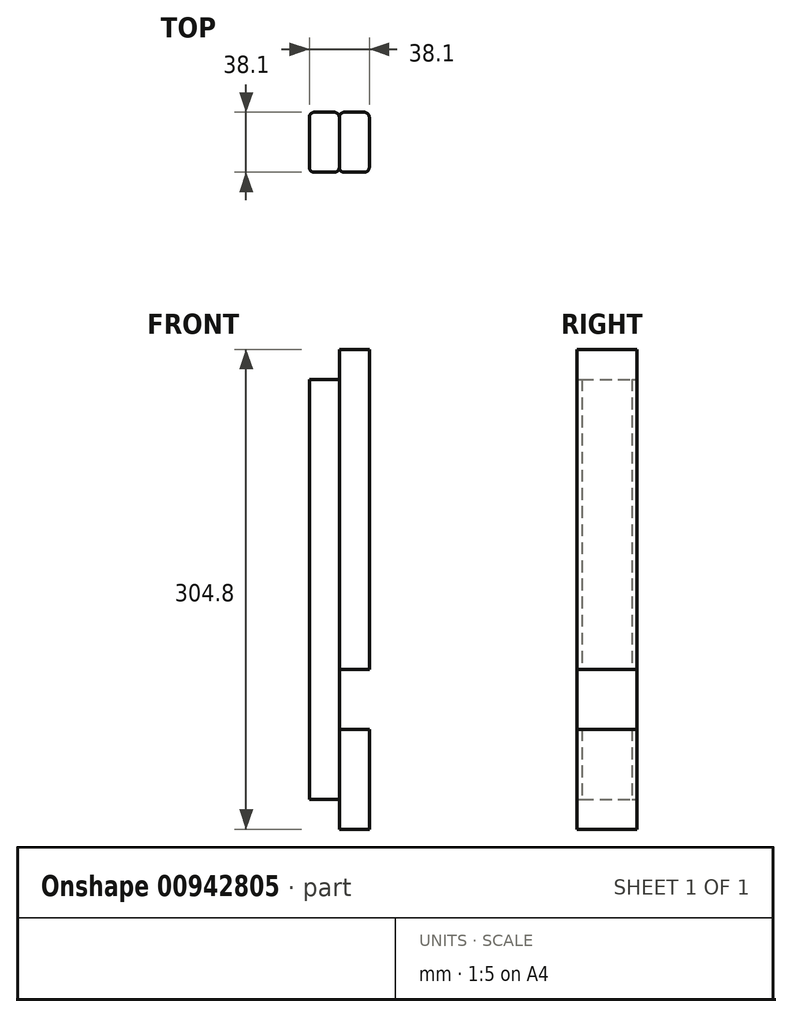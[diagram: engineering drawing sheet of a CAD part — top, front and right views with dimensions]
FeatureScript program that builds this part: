
annotation { "Feature Type Name" : "Feature", "Feature Type Description" : "" }
export const myFeature = defineFeature(function(context is Context, id is Id, definition is map)
    precondition{}
    {
        {
            var Q0;
            Q0=qCreatedBy(makeId("Top.planeOp"),FACE);
            var sketch = newSketch(context, id + "F0", { "sketchPlane" : qUnion([Q0])});
            skLineSegment(sketch, "E0.bottom", {"start": v(3.15, 0) * mm, "end": v(15.9, 0) * mm});
            skLineSegment(sketch, "E0.top", {"start": v(3.15, 38.1) * mm, "end": v(15.9, 38.1) * mm});
            skLineSegment(sketch, "E0.left", {"start": v(0, 3.15) * mm, "end": v(0, 34.95) * mm});
            skLineSegment(sketch, "E0.right", {"start": v(19.05, 3.15) * mm, "end": v(19.05, 34.95) * mm});
            skPoint(sketch, "E1.visualSharp", {"position": v(0, 38.1) * mm});
            skArc(sketch, "E1.filletArc", {"start": v(3.15, 38.1) * mm, "mid": v(0.92, 37.18) * mm, "end": v(0, 34.95) * mm});
            skArc(sketch, "E2.filletArc", {"start": v(19.05, 34.95) * mm, "mid": v(18.13, 37.18) * mm, "end": v(15.9, 38.1) * mm});
            skPoint(sketch, "E3.visualSharp", {"position": v(19.05, 0) * mm});
            skArc(sketch, "E3.filletArc", {"start": v(15.9, 0) * mm, "mid": v(18.13, 0.92) * mm, "end": v(19.05, 3.15) * mm});
            skPoint(sketch, "E4.visualSharp", {"position": v(0, 0) * mm});
            skArc(sketch, "E4.filletArc", {"start": v(0, 3.15) * mm, "mid": v(0.92, 0.92) * mm, "end": v(3.15, 0) * mm});
            skLineSegment(sketch, "E5.bottom", {"start": v(22.2, 0) * mm, "end": v(34.95, 0) * mm});
            skLineSegment(sketch, "E5.right", {"start": v(38.1, 3.15) * mm, "end": v(38.1, 34.95) * mm});
            skArc(sketch, "E6.filletArc", {"start": v(22.2, 38.1) * mm, "mid": v(19.97, 37.18) * mm, "end": v(19.05, 34.95) * mm});
            skArc(sketch, "E7.filletArc", {"start": v(38.1, 34.95) * mm, "mid": v(37.18, 37.18) * mm, "end": v(34.95, 38.1) * mm});
            skArc(sketch, "E8.filletArc", {"start": v(34.95, 0) * mm, "mid": v(37.18, 0.92) * mm, "end": v(38.1, 3.15) * mm});
            skArc(sketch, "E9.filletArc", {"start": v(19.05, 3.15) * mm, "mid": v(19.97, 0.92) * mm, "end": v(22.2, 0) * mm});
            skLineSegment(sketch, "E10", {"start": v(22.2, 38.1) * mm, "end": v(34.95, 38.1) * mm});
            skSolve(sketch);
        }
        {
            var Q0;
            Q0=makeQuery(id+"F0.imprint","IMPRINT",FACE,{"disambiguationData":[TD([[makeQuery(id+"F0.imprint","IMPRINT",EDGE,{"derivedFrom":sQuery(id+"F0.wireOp",EDGE,"E5.bottom")}),1.0]])]});
            var Q1;
            Q1=makeQuery(id+"F0.imprint","IMPRINT",FACE,{"disambiguationData":[TD([[makeQuery(id+"F0.imprint","IMPRINT",EDGE,{"derivedFrom":sQuery(id+"F0.wireOp",EDGE,"b7ff1907-7b2b-4cdd-8ea5-b45dade5522d.bottom")}),1.0]])]});
            var Q2;
            Q2=makeQuery(id+"F0.imprint","IMPRINT",FACE,{"disambiguationData":[TD([[makeQuery(id+"F0.imprint","IMPRINT",EDGE,{"derivedFrom":sQuery(id+"F0.wireOp",EDGE,"66c86851-db75-4c71-9093-7621e61d7ab7.bottom")}),1.0]])]});
            extrude(context, id + "F1", {"entities" : qUnion([Q0, Q1, Q2]), "depth" : 304.8 * mm, "offsetDistance" : 25.4 * mm});
        }
        {
            var Q0;
            Q0=qSketchRegion(id+"F0",true);
            extrude(context, id + "F2", {"entities" : qUnion([Q0]), "operationType" : NewBodyOperationType.ADD, "depth" : 285.75 * mm, "offsetDistance" : 25.4 * mm});
        }
        {
            var Q0;
            Q0=makeQuery(id+"F0.imprint","IMPRINT",FACE,{"disambiguationData":[TD([[makeQuery(id+"F0.imprint","IMPRINT",EDGE,{"derivedFrom":sQuery(id+"F0.wireOp",EDGE,"E0.bottom")}),1.0]])]});
            extrude(context, id + "F3", {"entities" : qUnion([Q0]), "operationType" : NewBodyOperationType.REMOVE, "depth" : 19.05 * mm, "offsetDistance" : 25.4 * mm});
        }
        {
            var Q0;
            Q0=makeQuery(id+"F1.opExtrude","SWEPT_FACE",FACE,{"disambiguationData":[OSD([sQuery(id+"F0.wireOp",EDGE,"E5.bottom")])]});
            var sketch = newSketch(context, id + "F4", { "sketchPlane" : qUnion([Q0])});
            skLineSegment(sketch, "E11.0", {"start": v(38.1, 304.8) * mm, "end": v(38.1, 0) * mm});
            skPoint(sketch, "E12.0", {"position": v(28.58, 0) * mm});
            skPoint(sketch, "E13.0", {"position": v(19.05, 0) * mm});
            skLineSegment(sketch, "E14.0", {"start": v(19.05, 19.05) * mm, "end": v(19.05, 0) * mm});
            skLineSegment(sketch, "E15.0", {"start": v(19.05, 285.75) * mm, "end": v(19.05, 19.05) * mm});
            skLineSegment(sketch, "E16.bottom", {"start": v(19.05, 63.5) * mm, "end": v(38.1, 63.5) * mm});
            skLineSegment(sketch, "E16.top", {"start": v(19.05, 101.6) * mm, "end": v(38.1, 101.6) * mm});
            skLineSegment(sketch, "E16.left", {"start": v(19.05, 63.5) * mm, "end": v(19.05, 101.6) * mm});
            skLineSegment(sketch, "E16.right", {"start": v(38.1, 63.5) * mm, "end": v(38.1, 101.6) * mm});
            skSolve(sketch);
        }
        {
            var Q0;
            Q0 = qSketchRegion(id + "F4", true);
            extrude(context, id + "F5", {"entities" : qUnion([Q0]), "operationType" : NewBodyOperationType.REMOVE, "endBound" : BoundingType.THROUGH_ALL, "oppositeDirection" : true, "depth" : 25.4 * mm, "offsetDistance" : 25.4 * mm});
        }
    });
